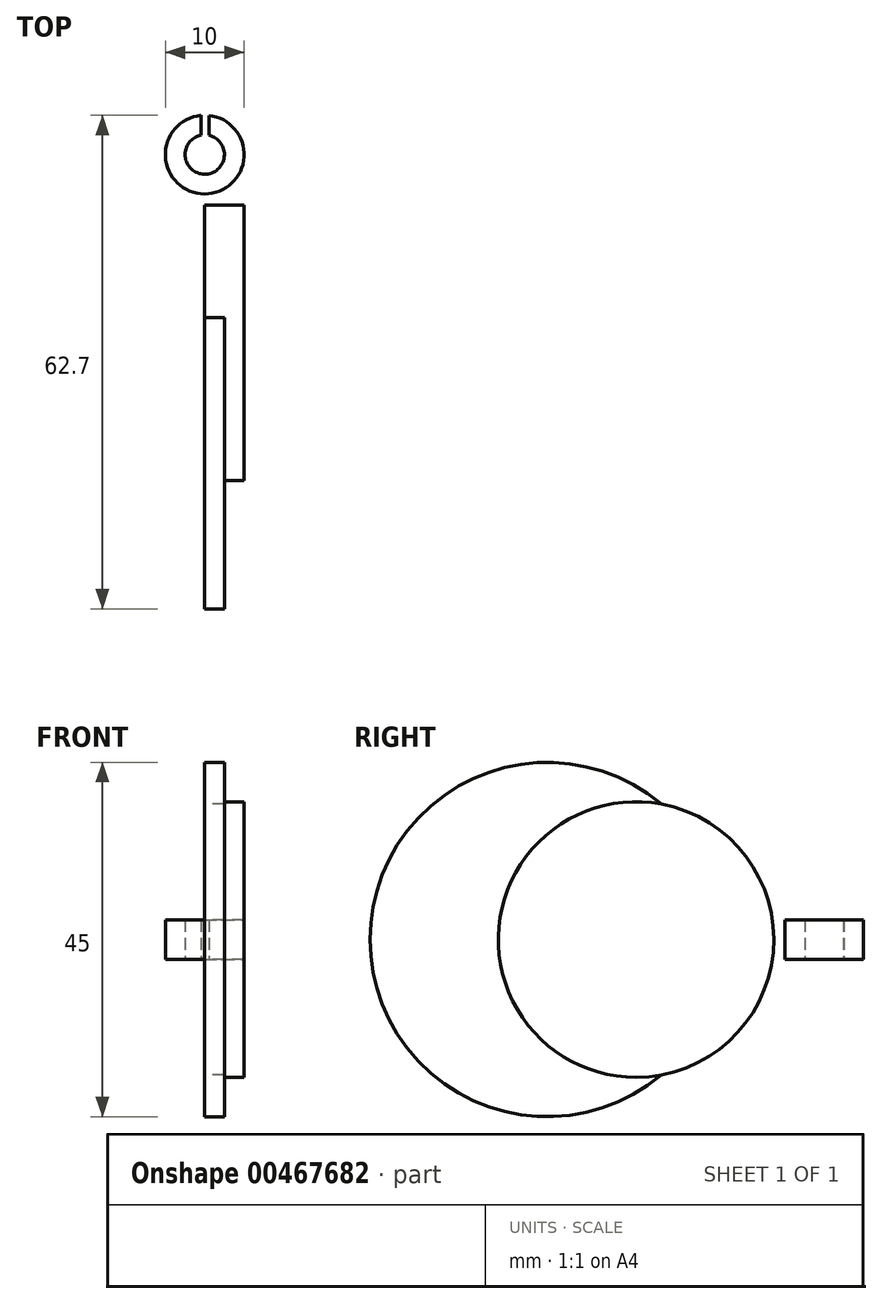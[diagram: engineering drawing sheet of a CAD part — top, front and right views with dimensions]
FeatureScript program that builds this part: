
annotation { "Feature Type Name" : "Feature", "Feature Type Description" : "" }
export const myFeature = defineFeature(function(context is Context, id is Id, definition is map)
    precondition{}
    {
        {
            var Q0;
            Q0=qCreatedBy(makeId("Top.planeOp"),FACE);
            var sketch = newSketch(context, id + "F0", { "sketchPlane" : qUnion([Q0])});
            skArc(sketch, "E0", {"start": v(-0.47, 4.98) * mm, "mid": v(-0.03, -5) * mm, "end": v(0.53, 4.97) * mm});
            skArc(sketch, "E1", {"start": v(-0.47, 2.46) * mm, "mid": v(-0.03, -2.5) * mm, "end": v(0.53, 2.44) * mm});
            skLineSegment(sketch, "E2", {"start": v(-0.47, 4.98) * mm, "end": v(-0.47, 2.46) * mm});
            skLineSegment(sketch, "E3", {"start": v(0.53, 4.97) * mm, "end": v(0.53, 2.44) * mm});
            skSolve(sketch);
        }
        {
            var Q0;
            Q0=makeQuery(id+"F0.imprint","IMPRINT",FACE,{"disambiguationData":[TD([[makeQuery(id+"F0.imprint","IMPRINT",EDGE,{"derivedFrom":sQuery(id+"F0.wireOp",EDGE,"E0")}),1.0]])]});
            extrude(context, id + "F1", {"entities" : qUnion([Q0]), "depth" : 5 * mm});
        }
        {
            var Q0;
            Q0=makeQuery(id+"F1.opExtrude","SWEPT_BODY",BODY,{"disambiguationData":[OSD([sQuery(id+"F0.wireOp",EDGE,"E0"),sQuery(id+"F0.wireOp",EDGE,"E1"),sQuery(id+"F0.wireOp",EDGE,"E2"),sQuery(id+"F0.wireOp",EDGE,"E3")])]});
            transform(context, id + "F2", {"entities" : qUnion([Q0]), "transformType" : TransformType.TRANSLATION_3D, "dx" : 0 * mm, "dy" : 0 * mm, "dz" : -2.5 * mm, "makeCopy" : false});
        }
        {
            var Q0;
            Q0=qCreatedBy(makeId("Right.planeOp"),FACE);
            var sketch = newSketch(context, id + "F3", { "sketchPlane" : qUnion([Q0])});
            skCircle(sketch, "E4", {"center": v(-23.93, 0) * mm, "radius": 17.5 * mm});
            skSolve(sketch);
        }
        {
            var Q0;
            Q0=qCreatedBy(makeId("Right.planeOp"),FACE);
            var sketch = newSketch(context, id + "F4", { "sketchPlane" : qUnion([Q0])});
            skCircle(sketch, "E5", {"center": v(-35.22, 0) * mm, "radius": 22.5 * mm});
            skSolve(sketch);
        }
        {
            var Q0;
            Q0 = qSketchRegion(id + "F3", true);
            extrude(context, id + "F5", {"entities" : qUnion([Q0]), "depth" : 5 * mm, "offsetDistance" : 25 * mm});
        }
        {
            var Q0;
            Q0 = qSketchRegion(id + "F4", true);
            extrude(context, id + "F6", {"entities" : qUnion([Q0]), "operationType" : NewBodyOperationType.ADD, "depth" : 2.5 * mm, "offsetDistance" : 25 * mm});
        }
    });
